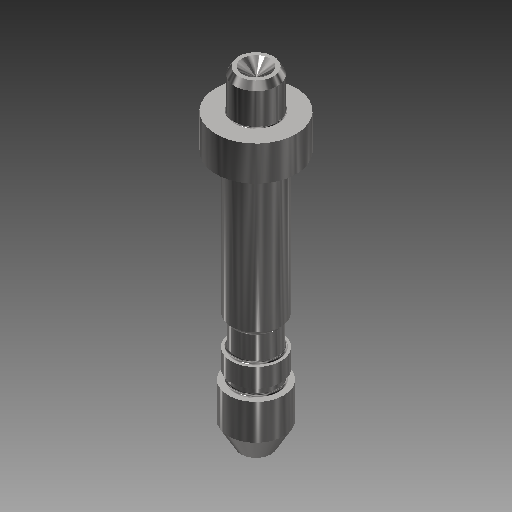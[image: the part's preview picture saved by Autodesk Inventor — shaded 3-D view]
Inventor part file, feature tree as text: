
AUTODESK INVENTOR PART (.ipt)
format: ipt  version: 2019 (Build 230136000, 136)  size: 186,880 bytes
history: native  units: mm
features: fillet x2, revolve x1, sketch x1
ambient origin geometry x8: Origin, YZ Plane, XZ Plane, XY Plane, X Axis, Y Axis, Z Axis, Center Point
bodies: Solid1 (feature_tree)
feature tree (4):
  revolve  "Revolution1"  [1 undecoded]
  fillet  "Fillet1"  Radius=1.2mm
  fillet  "Fillet2"  Radius=3.157mm
  sketch  "Sketch1"  dims[d0=7.0mm d1=3.85mm d2=1.2mm d3=3.157mm d4=6.108652mm d5=2.5mm d7=7.25mm d8=6.3mm d9=4.5mm d10=3.75mm d13=45.0deg d14=5.425mm d15=4.5mm d16=3.4mm d17=3.75mm d18=1.7mm d19=5.025mm d20=52.5mm d21=6.108652mm d22=30.0deg d23=6.4mm d24=90.0deg d25=0.5mm d26=0.25mm d28=0.944297mm d29=4.0mm]
note: 1 required parameter value undecoded (feature->parameter linkage not recoverable at this tier; creation-order binding heuristic only, values carry confidence <= 0.55)
